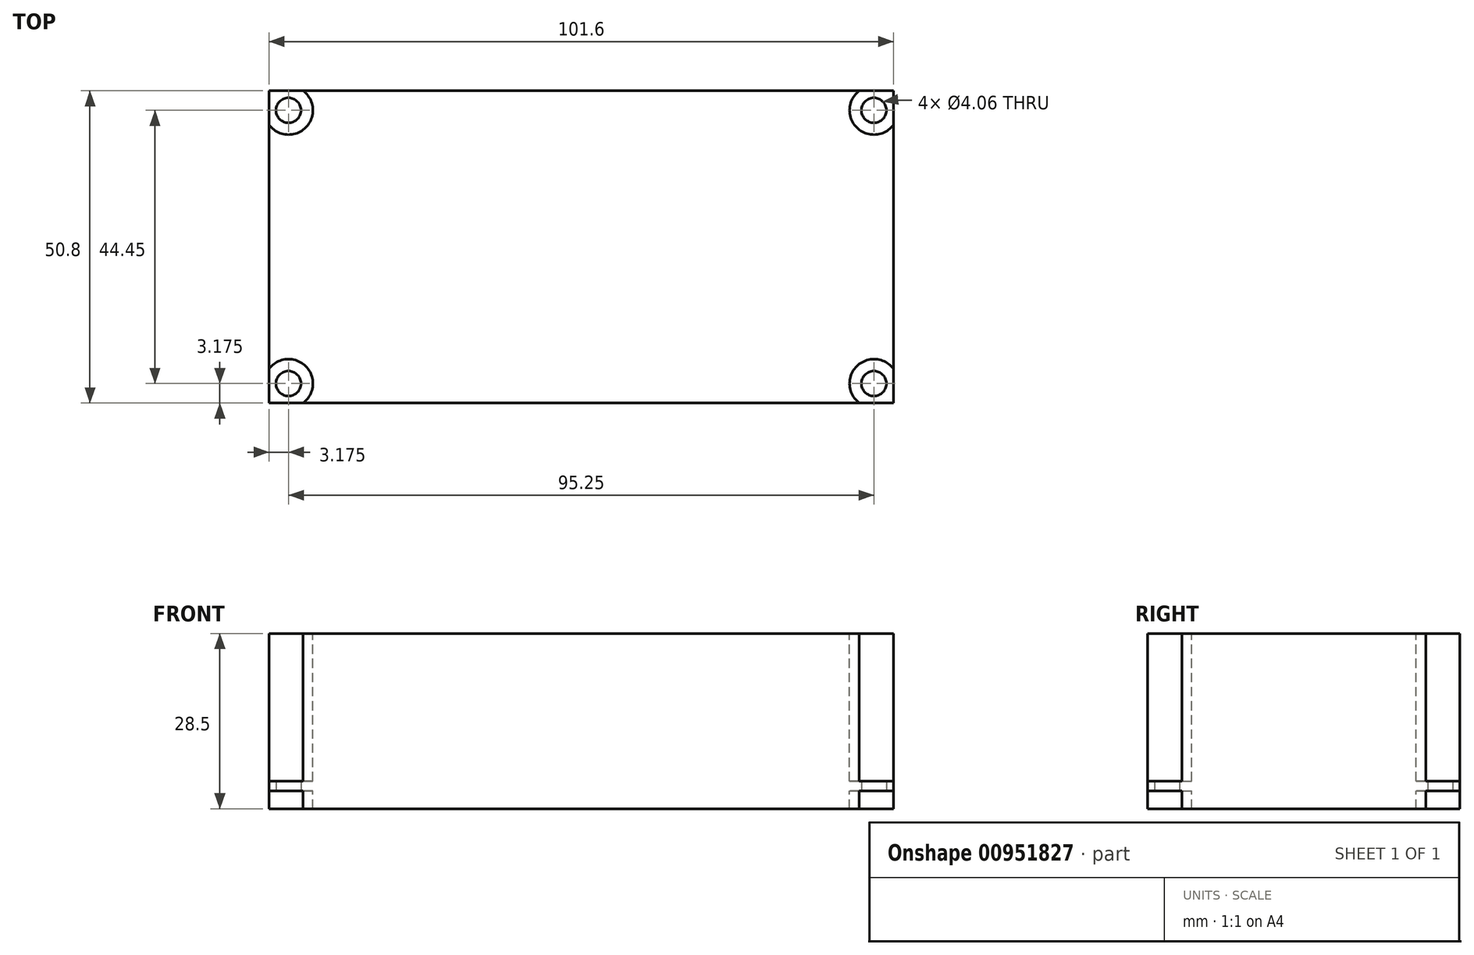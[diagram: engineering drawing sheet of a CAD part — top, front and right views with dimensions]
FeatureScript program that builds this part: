
annotation { "Feature Type Name" : "Feature", "Feature Type Description" : "" }
export const myFeature = defineFeature(function(context is Context, id is Id, definition is map)
    precondition{}
    {
        {
            var Q0;
            Q0=qCreatedBy(makeId("Top.planeOp"),FACE);
            var sketch = newSketch(context, id + "F0", { "sketchPlane" : qUnion([Q0])});
            skLineSegment(sketch, "E0.bottom", {"start": v(-50.8, 25.4) * mm, "end": v(50.8, 25.4) * mm});
            skLineSegment(sketch, "E0.top", {"start": v(-50.8, -25.4) * mm, "end": v(50.8, -25.4) * mm});
            skLineSegment(sketch, "E0.left", {"start": v(-50.8, 25.4) * mm, "end": v(-50.8, -25.4) * mm});
            skLineSegment(sketch, "E0.right", {"start": v(50.8, 25.4) * mm, "end": v(50.8, -25.4) * mm});
            skPoint(sketch, "E0.middle", {"position": v(0, 0) * mm});
            skLineSegment(sketch, "E1.bottom", {"start": v(-47.63, 22.23) * mm, "end": v(47.63, 22.23) * mm, "construction": true});
            skLineSegment(sketch, "E1.top", {"start": v(-47.63, -22.22) * mm, "end": v(47.62, -22.22) * mm, "construction": true});
            skLineSegment(sketch, "E1.left", {"start": v(-47.63, 22.23) * mm, "end": v(-47.63, -22.22) * mm, "construction": true});
            skLineSegment(sketch, "E1.right", {"start": v(47.63, 22.23) * mm, "end": v(47.62, -22.22) * mm, "construction": true});
            skCircle(sketch, "E2", {"center": v(-47.63, 22.23) * mm, "radius": 2.03 * mm});
            skCircle(sketch, "E3", {"center": v(-47.63, -22.22) * mm, "radius": 2.03 * mm});
            skCircle(sketch, "E4", {"center": v(47.62, -22.22) * mm, "radius": 2.03 * mm});
            skCircle(sketch, "E5", {"center": v(47.63, 22.23) * mm, "radius": 2.03 * mm});
            skSolve(sketch);
        }
        {
            var Q0;
            Q0=makeQuery(id+"F0.imprint","IMPRINT",FACE,{"disambiguationData":[TD([[makeQuery(id+"F0.imprint","IMPRINT",EDGE,{"derivedFrom":sQuery(id+"F0.wireOp",EDGE,"E0.bottom")}),-1.0]])]});
            extrude(context, id + "F1", {"entities" : qUnion([Q0]), "depth" : 1.63 * mm});
        }
        {
            var Q0;
            Q0=makeQuery(id+"F1.opExtrude","CAP_FACE",FACE,{"disambiguationData":[OSD([sQuery(id+"F0.wireOp",EDGE,"E0.bottom"),sQuery(id+"F0.wireOp",EDGE,"E0.top"),sQuery(id+"F0.wireOp",EDGE,"E0.left"),sQuery(id+"F0.wireOp",EDGE,"E0.right"),sQuery(id+"F0.wireOp",EDGE,"E2"),sQuery(id+"F0.wireOp",EDGE,"E3"),sQuery(id+"F0.wireOp",EDGE,"E4"),sQuery(id+"F0.wireOp",EDGE,"E5")])],"isStart":true});
            var sketch = newSketch(context, id + "F2", { "sketchPlane" : qUnion([Q0])});
            skLineSegment(sketch, "E6.bottom", {"start": v(45.25, -25.4) * mm, "end": v(-45.25, -25.4) * mm});
            skLineSegment(sketch, "E6.top", {"start": v(45.25, 25.4) * mm, "end": v(-45.25, 25.4) * mm});
            skPoint(sketch, "E6.middle", {"position": v(0, 0) * mm});
            skArc(sketch, "E7", {"start": v(45.25, 25.4) * mm, "mid": v(44.82, 19.42) * mm, "end": v(50.8, 19.85) * mm});
            skArc(sketch, "E8", {"start": v(50.8, -19.85) * mm, "mid": v(44.82, -19.42) * mm, "end": v(45.25, -25.4) * mm});
            skArc(sketch, "E9", {"start": v(-45.25, -25.4) * mm, "mid": v(-44.82, -19.42) * mm, "end": v(-50.8, -19.85) * mm});
            skArc(sketch, "E10", {"start": v(-50.8, 19.85) * mm, "mid": v(-44.82, 19.42) * mm, "end": v(-45.25, 25.4) * mm});
            skPoint(sketch, "E11.trimOffspring.end.orphan", {"position": v(50.8, 25.4) * mm});
            skLineSegment(sketch, "E12.trimOffspring", {"start": v(50.8, -19.85) * mm, "end": v(50.8, 19.85) * mm});
            skPoint(sketch, "E13.orphan", {"position": v(50.8, -25.4) * mm});
            skPoint(sketch, "E14.orphan", {"position": v(-50.8, 25.4) * mm});
            skLineSegment(sketch, "E15.trimOffspring", {"start": v(-50.8, -19.85) * mm, "end": v(-50.8, 19.85) * mm});
            skPoint(sketch, "E16.trimOffspring.end.orphan", {"position": v(-50.8, -25.4) * mm});
            skSolve(sketch);
        }
        {
            var Q0;
            Q0=qSketchRegion(id+"F2",true);
            extrude(context, id + "F3", {"entities" : qUnion([Q0]), "operationType" : NewBodyOperationType.ADD, "depth" : 2.87 * mm, "hasSecondDirection" : true, "secondDirectionOppositeDirection" : true, "secondDirectionDepth" : 25.63 * mm});
        }
    });
